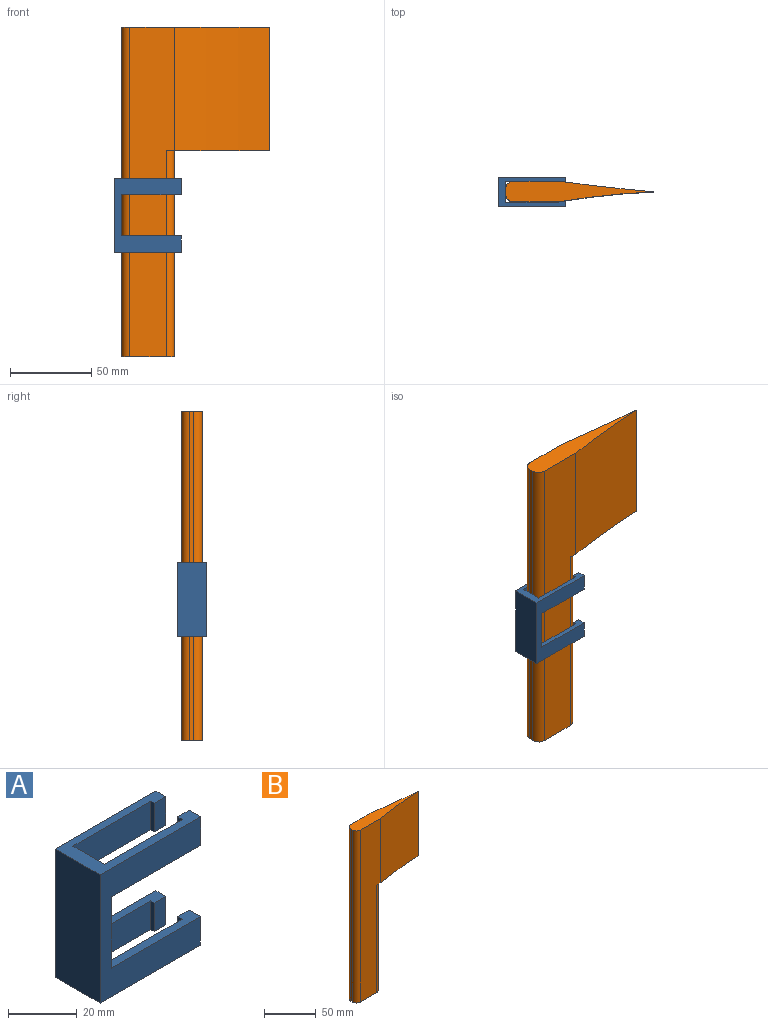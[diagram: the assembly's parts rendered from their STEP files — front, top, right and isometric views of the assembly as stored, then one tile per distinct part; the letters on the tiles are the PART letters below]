
ASSEMBLY  parts=2 mates=1
PART A: 26 faces, bbox 41.4x18.4x45.7 mm
  f0: plane 10.16x1.49mm, normal (-1,0,0), area 15.1mm2, adj f1,f11,f12,f13
  f1: plane 32x10.16mm, normal (0,-1,0), area 325.1mm2, adj f0,f2,f12,f13
  f2: plane 12.98x10.16mm, normal (1,0,0), area 131.8mm2, adj f1,f3,f12,f13
  f3: plane 32x10.16mm, normal (0,1,0), area 325.1mm2, adj f2,f4,f12,f13
  f4: plane 10.16x1.85mm, normal (-1,0,0), area 18.8mm2, adj f3,f5,f12,f13
  f5: plane 10.16x4.74mm, normal (0,1,0), area 48.2mm2, adj f4,f6,f12,f13
  f6: plane 10.16x4.69mm, normal (1,0,0), area 47.7mm2, adj f5,f7,f12,f13
  f7: plane 45.72x41.38mm, normal (0,-1,0), area 956.6mm2, adj f6,f8,f12,f13,f14,f16,f24,f25
  f8: plane 45.72x18.4mm, normal (-1,0,0), area 841.1mm2, adj f7,f9,f13,f25
  f9: plane 45.72x41.38mm, normal (0,1,0), area 957mm2, adj f8,f10,f12,f13,f14,f15,f17,f25
  f10: plane 10.16x4.07mm, normal (1,0,0), area 41.4mm2, adj f9,f11,f12,f13
  f11: plane 10.16x4.74mm, normal (0,-1,0), area 48.2mm2, adj f0,f10,f12,f13
  f12: plane 36.79x18.4mm, normal (0,0,-1), area 216mm2, adj f0,f1,f2,f3,f4,f5,f6,f7
  f13: plane 41.38x18.4mm, normal (0,0,1), area 300.3mm2, adj f0,f1,f2,f3,f4,f5,f6,f7
  f14: plane 35.56x18.4mm, normal (1,0,0), area 599.1mm2, adj f7,f9,f12,f15,f16,f20,f21,f25
  f15: plane 36.79x4.07mm, normal (0,0,1), area 102.4mm2, adj f9,f14,f17,f18,f19,f20
  f16: plane 36.74x4.66mm, normal (0,0,1), area 112.7mm2, adj f7,f14,f21,f22,f23,f24
  f17: plane 10.16x4.07mm, normal (1,0,0), area 41.4mm2, adj f9,f15,f18,f25
  f18: plane 10.16x4.73mm, normal (0,-1,0), area 48mm2, adj f15,f17,f19,f25
  f19: plane 10.16x1.48mm, normal (-1,0,0), area 15mm2, adj f15,f18,f20,f25
  f20: plane 32.06x10.16mm, normal (0,-1,0), area 325.7mm2, adj f14,f15,f19,f25
  f21: plane 32.05x10.16mm, normal (0,1,0), area 325.6mm2, adj f14,f16,f22,f25
  f22: plane 10.16x1.83mm, normal (-1,0,0), area 18.6mm2, adj f16,f21,f23,f25
  f23: plane 10.16x4.7mm, normal (0,1,0), area 47.7mm2, adj f16,f22,f24,f25
  f24: plane 10.16x4.66mm, normal (1,0,0), area 47.4mm2, adj f7,f16,f23,f25
  f25: plane 41.37x18.4mm, normal (0,0,-1), area 299.4mm2, adj f7,f8,f9,f14,f17,f18,f19,f20
PART B: 13 faces, bbox 91.4x12.7x203.2 mm
  f0: plane 63.89x12.74mm, normal (0,0,-1), area 336.6mm2, adj f1,f2,f3,f5,f7,f9,f10
  f1: cylinder r=480.78mm len=76.2mm, axis (0,0,1), area 4508.6mm2, adj f0,f2,f5,f6
  f2: cylinder r=1295.9mm len=76.2mm, axis (0,0,1), area 4510.2mm2, adj f0,f1,f3,f6
  f3: plane 203.2x27.51mm, normal (0,1,0), area 4945.3mm2, adj f0,f2,f6,f8,f10,f11
  f4: plane 203.2x2.58mm, normal (-1,0,0), area 524.8mm2, adj f6,f8,f11,f12
  f5: plane 203.2x27.51mm, normal (0,-1,0), area 4945.3mm2, adj f0,f1,f6,f8,f9,f12
  f6: plane 91.41x12.74mm, normal (0,0,1), area 729.7mm2, adj f1,f2,f3,f4,f5,f11,f12
  f7: plane 127x2.58mm, normal (1,0,0), area 328mm2, adj f0,f8,f9,f10
  f8: plane 32.59x12.74mm, normal (0,0,-1), area 393.2mm2, adj f3,f4,f5,f7,f9,f10,f11,f12
  f9: cylinder r=5.08mm len=127mm, axis (0,0,1), area 1013.4mm2, adj f0,f5,f7,f8
  f10: cylinder r=5.08mm len=127mm, axis (0,0,-1), area 1013.4mm2, adj f0,f3,f7,f8
  f11: cylinder r=5.08mm len=203.2mm, axis (0,0,-1), area 1621.5mm2, adj f3,f4,f6,f8
  f12: cylinder r=5.08mm len=203.2mm, axis (0,0,1), area 1621.5mm2, adj f4,f5,f6,f8
PLACE A t=(-21.07,-26.02,84.2)mm
PLACE B t=(-21.13,-26.15,-25.92)mm
MATE slider B.f8 <-> A.f25  axis (0,0,-1) through (-37.18,-25.9,-152.92)mm
